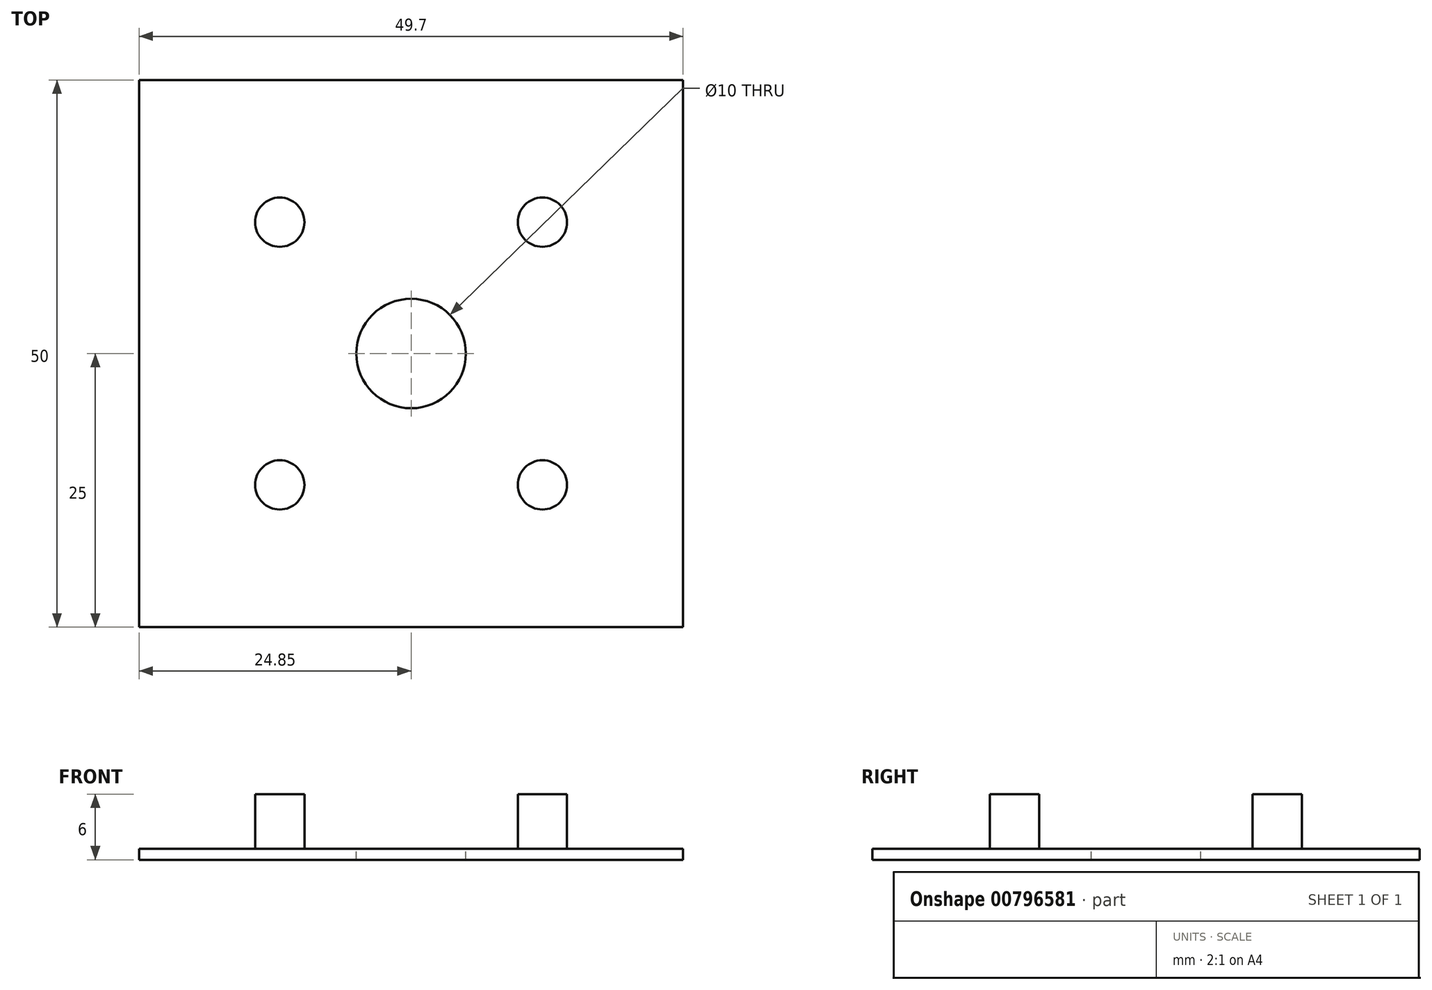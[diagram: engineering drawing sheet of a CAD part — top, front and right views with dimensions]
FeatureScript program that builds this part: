
annotation { "Feature Type Name" : "Feature", "Feature Type Description" : "" }
export const myFeature = defineFeature(function(context is Context, id is Id, definition is map)
    precondition{}
    {
        {
            var Q0;
            Q0=qCreatedBy(makeId("Top.planeOp"),FACE);
            var sketch = newSketch(context, id + "F0", { "sketchPlane" : qUnion([Q0])});
            skLineSegment(sketch, "E0.bottom", {"start": v(24.85, 25) * mm, "end": v(-24.85, 25) * mm});
            skLineSegment(sketch, "E0.top", {"start": v(24.85, -25) * mm, "end": v(-24.85, -25) * mm});
            skLineSegment(sketch, "E0.left", {"start": v(24.85, 25) * mm, "end": v(24.85, -25) * mm});
            skLineSegment(sketch, "E0.right", {"start": v(-24.85, 25) * mm, "end": v(-24.85, -25) * mm});
            skPoint(sketch, "E0.middle", {"position": v(0, 0) * mm});
            skSolve(sketch);
        }
        {
            var Q0;
            Q0=makeQuery(id+"F0.imprint","IMPRINT",FACE,{"disambiguationData":[TD([[makeQuery(id+"F0.imprint","IMPRINT",EDGE,{"derivedFrom":sQuery(id+"F0.wireOp",EDGE,"E0.bottom")}),1.0]])]});
            extrude(context, id + "F1", {"entities" : qUnion([Q0]), "depth" : 1 * mm, "offsetDistance" : 25 * mm});
        }
        {
            var Q0;
            Q0=makeQuery(id+"F1.opExtrude","CAP_FACE",FACE,{"disambiguationData":[OSD([sQuery(id+"F0.wireOp",EDGE,"E0.bottom"),sQuery(id+"F0.wireOp",EDGE,"E0.top"),sQuery(id+"F0.wireOp",EDGE,"E0.left"),sQuery(id+"F0.wireOp",EDGE,"E0.right")])],"isStart":false});
            var sketch = newSketch(context, id + "F2", { "sketchPlane" : qUnion([Q0])});
            skCircle(sketch, "E1", {"center": v(-12, 12) * mm, "radius": 2.25 * mm});
            skCircle(sketch, "E2.1.0", {"center": v(-12, -12) * mm, "radius": 2.25 * mm});
            skCircle(sketch, "E2.2.0", {"center": v(12, -12) * mm, "radius": 2.25 * mm});
            skCircle(sketch, "E2.3.0", {"center": v(12, 12) * mm, "radius": 2.25 * mm});
            skPoint(sketch, "E2.center", {"position": v(0, 0) * mm});
            skSolve(sketch);
        }
        {
            var Q0;
            Q0=makeQuery(id+"F2.imprint","IMPRINT",FACE,{"disambiguationData":[TD([[makeQuery(id+"F2.imprint","IMPRINT",EDGE,{"derivedFrom":sQuery(id+"F2.wireOp",EDGE,"E1")}),1.0]])]});
            var Q1;
            Q1=makeQuery(id+"F2.imprint","IMPRINT",FACE,{"disambiguationData":[TD([[makeQuery(id+"F2.imprint","IMPRINT",EDGE,{"derivedFrom":sQuery(id+"F2.wireOp",EDGE,"E2.3.0")}),1.0]])]});
            var Q2;
            Q2=makeQuery(id+"F2.imprint","IMPRINT",FACE,{"disambiguationData":[TD([[makeQuery(id+"F2.imprint","IMPRINT",EDGE,{"derivedFrom":sQuery(id+"F2.wireOp",EDGE,"E2.1.0")}),1.0]])]});
            var Q3;
            Q3=makeQuery(id+"F2.imprint","IMPRINT",FACE,{"disambiguationData":[TD([[makeQuery(id+"F2.imprint","IMPRINT",EDGE,{"derivedFrom":sQuery(id+"F2.wireOp",EDGE,"E2.2.0")}),1.0]])]});
            extrude(context, id + "F3", {"entities" : qUnion([Q0, Q1, Q2, Q3]), "operationType" : NewBodyOperationType.ADD, "depth" : 5 * mm, "offsetDistance" : 25 * mm});
        }
        {
            var Q0;
            Q0=makeQuery(id+"F1.opExtrude","CAP_FACE",FACE,{"disambiguationData":[OSD([sQuery(id+"F0.wireOp",EDGE,"E0.bottom"),sQuery(id+"F0.wireOp",EDGE,"E0.top"),sQuery(id+"F0.wireOp",EDGE,"E0.left"),sQuery(id+"F0.wireOp",EDGE,"E0.right")])],"isStart":false});
            var sketch = newSketch(context, id + "F4", { "sketchPlane" : qUnion([Q0])});
            skCircle(sketch, "E3", {"center": v(0, 0) * mm, "radius": 5 * mm});
            skSolve(sketch);
        }
        {
            var Q0;
            Q0=makeQuery(id+"F4.imprint","IMPRINT",FACE,{"disambiguationData":[TD([[makeQuery(id+"F4.imprint","IMPRINT",EDGE,{"derivedFrom":sQuery(id+"F4.wireOp",EDGE,"E3")}),1.0]])]});
            extrude(context, id + "F5", {"entities" : qUnion([Q0]), "operationType" : NewBodyOperationType.REMOVE, "oppositeDirection" : true, "depth" : 25 * mm, "offsetDistance" : 25 * mm});
        }
    });
